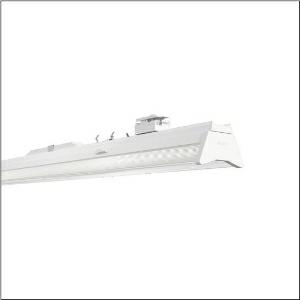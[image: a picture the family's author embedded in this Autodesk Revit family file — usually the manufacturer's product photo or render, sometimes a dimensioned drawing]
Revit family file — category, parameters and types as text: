
# Revit family: licross_r__11_performance_mo_51td16dn4axg_9e80
name_source: partatom
category: Lighting Fixtures
units: mm (PartAtom-declared; Revit-internal decimal feet)

## family parameters
Cut with Voids When Loaded = No
Host = Face
Light Source = No
Part Type = Normal
Room Calculation Point = No
Round Connector Dimension = Use Diameter
Shared = No

## types (1)
- --- (1 x LED, 10110 lm, 57.1 W, 4000K)
    Apparent Load = 57 VA
    CIE Flux Codes = 66 88 96 79 100
    Color Rendering = 80
    Color Temperature = 4000K
    Default Elevation = 1800 mm
    Description = Licross® 11 Performance MO, luminaire insert, of sheet steel, galvanised, coil coated, white, length: 1.500mm, width: 120mm, height: 123mm, LED rated luminous flux: 10.110lm, light colour: 840, control gear: DALI 2, with plug, 5-pole, with phase selection, mains connection: 220..240V, AC, 50/60Hz, rated input power: 57W, internal wiring halogen-free, primary light control with lens, of plastic, primary optical cover: cover, of PMMA, light emission: direct/indirect distribution, primary light characteristic: symmetric, protection rating (complete): IP54, insulation class (complete): insulation class I (protective earthing), certification: CE, ENEC, VDE, UKCA, protection symbol: D if used in an environment with non-conductive dust loads with corresponding accessories, impact resistance: IK06, permissible ambient temperature for indoor applications: -25..+35°C, corresponds to IFS (International Featured Standards) requirements for safety and quality in the food industry, reducing of maximum allowable ambient temperature of 5°C with ceiling mounting, LABS conformity tested according to VDMA 24364:2018-05, packaging unit: 1 piece
    Height = 114 mm
    Lamp = 1 x LED
    Lamp Light Flux = 10110 lm
    Lamp Power = 57.1 W
    Lamp count = 1
    Length = 1500 mm
    Luminous efficacy = 177 lm/W
    Manufacturer = Siteco
    ModVariant = No
    Model = 51TD16DN4AXG
    Mounting Place = Ceiling
    Mounting Type = Pendant
    Number of Poles = 1
    OnlyDefault = Yes
    Power Factor = 1
    Product Name = Licross® 11 Performance MO
    Product group = luminaire insert | ceiling pendant
    ProductGroupID = 902
    Protection Class = Protection class I
    Protection Degree = IP 54
    RLX_Detail_Level = 1
    RLX_Emergency_Light_Flux = 0 lm
    RLX_Emergency_Type = 0
    RLX_Emergency_Type_DB = No
    RlxData = <blob elided: 34113 chars, md5=eea8dbed>
    Socket = socket
    Standby Power = 0 W
    System Light Flux = 10110 lm
    System Power = 57 W
    Type Comments = factory setting: luminous flux: 100 % | dim-lin: 254 | 378 mA
    Type Image = l_1256138.jpg
    URL = http://relux.com
    VarID = @adj_122701
    Voltage = 0 V
    Weight = 0.00 kg
    Width = 120 mm

## geometry (parser evidence)
native form markers: Blend x4, Sweep x12
no freeform markers — native parametric forms only
